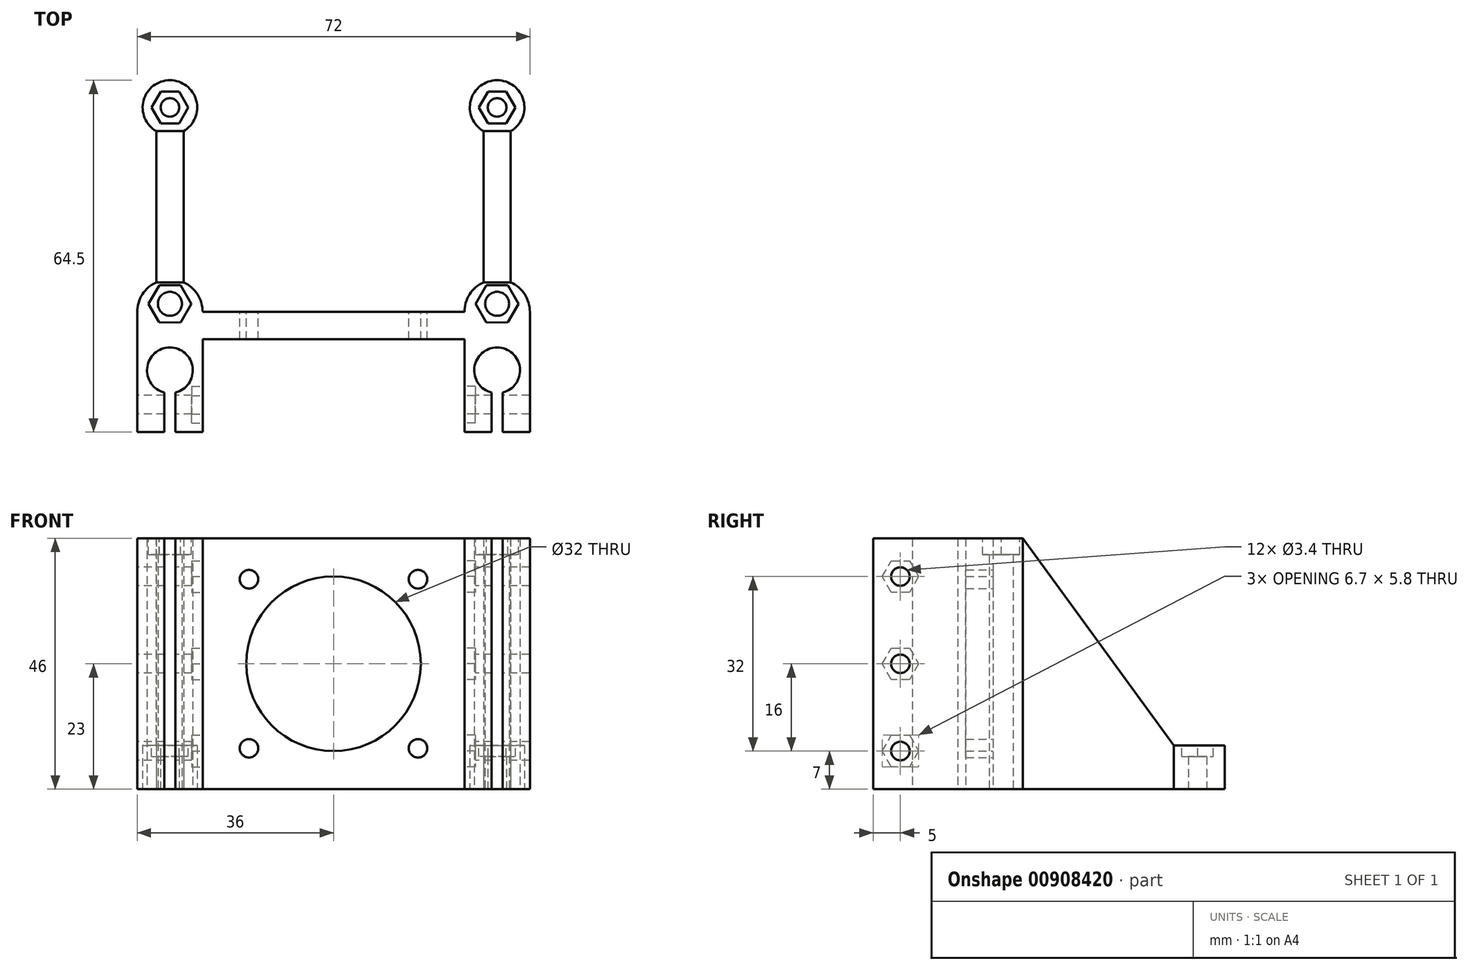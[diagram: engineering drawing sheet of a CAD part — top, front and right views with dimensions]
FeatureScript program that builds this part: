
annotation { "Feature Type Name" : "Feature", "Feature Type Description" : "" }
export const myFeature = defineFeature(function(context is Context, id is Id, definition is map)
    precondition{}
    {
        {
            var Q0;
            Q0=qCreatedBy(makeId("Top.planeOp"),FACE);
            var sketch = newSketch(context, id + "F0", { "sketchPlane" : qUnion([Q0])});
            skArc(sketch, "E0", {"start": v(-29, -14.78) * mm, "mid": v(-30, -6.5) * mm, "end": v(-31, -14.78) * mm});
            skPoint(sketch, "E0.first.point", {"position": v(-31.13, -14.74) * mm});
            skPoint(sketch, "E0.second.point", {"position": v(-34.04, -9.56) * mm});
            skPoint(sketch, "E0.third.point", {"position": v(-26.15, -9.02) * mm});
            skPoint(sketch, "E1.first.point", {"position": v(-36, 0) * mm});
            skLineSegment(sketch, "E2", {"start": v(-36, 0) * mm, "end": v(-36, -22) * mm});
            skLineSegment(sketch, "E3", {"start": v(-36, -22) * mm, "end": v(-31, -22) * mm});
            skLineSegment(sketch, "E4", {"start": v(-31, -22) * mm, "end": v(-31, -14.78) * mm});
            skLineSegment(sketch, "E5", {"start": v(-29, -14.78) * mm, "end": v(-29, -22) * mm});
            skLineSegment(sketch, "E6", {"start": v(-29, -22) * mm, "end": v(-24, -22) * mm});
            skLineSegment(sketch, "E7", {"start": v(0, 0) * mm, "end": v(-24, 0) * mm});
            skLineSegment(sketch, "E8", {"start": v(0, 0) * mm, "end": v(0, -5) * mm});
            skLineSegment(sketch, "E9", {"start": v(0, -5) * mm, "end": v(-24, -5) * mm});
            skLineSegment(sketch, "E10", {"start": v(-24, -5) * mm, "end": v(-24, -22) * mm});
            skLineSegment(sketch, "E11", {"start": v(-30, -10.7) * mm, "end": v(-30, 1.5) * mm, "construction": true});
            skLineSegment(sketch, "E12", {"start": v(-24, 0) * mm, "end": v(-36, 0) * mm, "construction": true});
            skArc(sketch, "E13", {"start": v(-24, 0) * mm, "mid": v(-30, 6) * mm, "end": v(-36, 0) * mm});
            skPoint(sketch, "E14.MirrorP", {"position": v(34.04, -9.56) * mm});
            skLineSegment(sketch, "E15.MirrorCS", {"start": v(0, -5) * mm, "end": v(24, -5) * mm});
            skLineSegment(sketch, "E16.MirrorCS", {"start": v(24, 0) * mm, "end": v(36, 0) * mm, "construction": true});
            skLineSegment(sketch, "E17.MirrorCS", {"start": v(29, -22) * mm, "end": v(24, -22) * mm});
            skPoint(sketch, "E18.MirrorP", {"position": v(26.15, -9.02) * mm});
            skLineSegment(sketch, "E19.MirrorCS", {"start": v(31, -22) * mm, "end": v(31, -14.78) * mm});
            skLineSegment(sketch, "E20.MirrorCS", {"start": v(29, -14.78) * mm, "end": v(29, -22) * mm});
            skPoint(sketch, "E21.MirrorP", {"position": v(31.13, -14.74) * mm});
            skPoint(sketch, "E22.MirrorP", {"position": v(36, 0) * mm});
            skArc(sketch, "E23.MirrorCS", {"start": v(24, 0) * mm, "mid": v(30, 6) * mm, "end": v(36, 0) * mm});
            skArc(sketch, "E24.MirrorC", {"start": v(29, -14.78) * mm, "mid": v(30, -6.5) * mm, "end": v(31, -14.78) * mm});
            skLineSegment(sketch, "E25.MirrorCS", {"start": v(0, 0) * mm, "end": v(24, 0) * mm});
            skLineSegment(sketch, "E26.MirrorCS", {"start": v(24, -5) * mm, "end": v(24, -22) * mm});
            skLineSegment(sketch, "E27.MirrorCS", {"start": v(30, -10.7) * mm, "end": v(30, 1.5) * mm, "construction": true});
            skLineSegment(sketch, "E28.MirrorCS", {"start": v(36, -22) * mm, "end": v(31, -22) * mm});
            skLineSegment(sketch, "E29.MirrorCS", {"start": v(36, 0) * mm, "end": v(36, -22) * mm});
            skCircle(sketch, "E30", {"center": v(-30, 1.5) * mm, "radius": 2.2 * mm});
            skCircle(sketch, "E31.MirrorC", {"center": v(30, 1.5) * mm, "radius": 2.2 * mm});
            skLineSegment(sketch, "E32", {"start": v(-30, 1.5) * mm, "end": v(-30, 46.69) * mm, "construction": true});
            skLineSegment(sketch, "E33", {"start": v(-32.5, 5.45) * mm, "end": v(-32.5, 33.17) * mm});
            skLineSegment(sketch, "E34", {"start": v(-32.5, 33.17) * mm, "end": v(-27.5, 33.17) * mm});
            skLineSegment(sketch, "E35", {"start": v(-27.5, 33.17) * mm, "end": v(-27.5, 5.45) * mm});
            skLineSegment(sketch, "E36", {"start": v(-27.5, 5.45) * mm, "end": v(-32.5, 5.45) * mm, "construction": true});
            skCircle(sketch, "E37", {"center": v(-30, 37.5) * mm, "radius": 1.7 * mm});
            skCircle(sketch, "E38", {"center": v(-30, 37.5) * mm, "radius": 5 * mm});
            skLineSegment(sketch, "E39.MirrorCS", {"start": v(27.5, 33.17) * mm, "end": v(27.5, 5.45) * mm});
            skLineSegment(sketch, "E40.MirrorCS", {"start": v(32.5, 5.45) * mm, "end": v(32.5, 33.17) * mm});
            skCircle(sketch, "E41.MirrorC", {"center": v(30, 37.5) * mm, "radius": 5 * mm});
            skCircle(sketch, "E42.MirrorC", {"center": v(30, 37.5) * mm, "radius": 1.7 * mm});
            skSolve(sketch);
        }
        {
            var Q0;
            Q0=qSketchRegion(id+"F0",true);
            extrude(context, id + "F1", {"entities" : qUnion([Q0]), "depth" : 46 * mm, "offsetDistance" : 25 * mm});
        }
        {
            var Q0;
            Q0=makeQuery(id+"F1.opExtrude","CAP_FACE",FACE,{"disambiguationData":[OSD([sQuery(id+"F0.wireOp",EDGE,"E0"),sQuery(id+"F0.wireOp",EDGE,"E2"),sQuery(id+"F0.wireOp",EDGE,"E3"),sQuery(id+"F0.wireOp",EDGE,"E4"),sQuery(id+"F0.wireOp",EDGE,"E5"),sQuery(id+"F0.wireOp",EDGE,"E6"),sQuery(id+"F0.wireOp",EDGE,"E7"),sQuery(id+"F0.wireOp",EDGE,"E9"),sQuery(id+"F0.wireOp",EDGE,"E10"),sQuery(id+"F0.wireOp",EDGE,"E13"),sQuery(id+"F0.wireOp",EDGE,"E15.MirrorCS"),sQuery(id+"F0.wireOp",EDGE,"E17.MirrorCS"),sQuery(id+"F0.wireOp",EDGE,"E19.MirrorCS"),sQuery(id+"F0.wireOp",EDGE,"E20.MirrorCS"),sQuery(id+"F0.wireOp",EDGE,"E23.MirrorCS"),sQuery(id+"F0.wireOp",EDGE,"E24.MirrorC"),sQuery(id+"F0.wireOp",EDGE,"E25.MirrorCS"),sQuery(id+"F0.wireOp",EDGE,"E26.MirrorCS"),sQuery(id+"F0.wireOp",EDGE,"E28.MirrorCS"),sQuery(id+"F0.wireOp",EDGE,"E29.MirrorCS"),sQuery(id+"F0.wireOp",EDGE,"E30"),sQuery(id+"F0.wireOp",EDGE,"E31.MirrorC")])],"isStart":false});
            var sketch = newSketch(context, id + "F2", { "sketchPlane" : qUnion([Q0])});
            skCircle(sketch, "E43.cCircle", {"center": v(-30, 1.5) * mm, "radius": 3.4 * mm, "construction": true});
            skLineSegment(sketch, "E43.0", {"start": v(-26.07, 1.48) * mm, "end": v(-28.05, -1.9) * mm});
            skLineSegment(sketch, "E43.1", {"start": v(-28.05, -1.9) * mm, "end": v(-31.98, -1.9) * mm});
            skLineSegment(sketch, "E43.2", {"start": v(-31.98, -1.9) * mm, "end": v(-33.93, 1.52) * mm});
            skLineSegment(sketch, "E43.3", {"start": v(-33.93, 1.52) * mm, "end": v(-31.95, 4.9) * mm});
            skLineSegment(sketch, "E43.4", {"start": v(-31.95, 4.9) * mm, "end": v(-28.02, 4.9) * mm});
            skLineSegment(sketch, "E43.5", {"start": v(-28.02, 4.9) * mm, "end": v(-26.07, 1.48) * mm});
            skPoint(sketch, "E43.0.midPoint", {"position": v(-27.06, -0.21) * mm});
            skPoint(sketch, "E44.MirrorP", {"position": v(27.06, -0.21) * mm});
            skLineSegment(sketch, "E45.MirrorCS", {"start": v(31.95, 4.9) * mm, "end": v(28.02, 4.9) * mm});
            skLineSegment(sketch, "E46.MirrorCS", {"start": v(28.05, -1.9) * mm, "end": v(31.98, -1.9) * mm});
            skLineSegment(sketch, "E47.MirrorCS", {"start": v(31.98, -1.9) * mm, "end": v(33.93, 1.52) * mm});
            skCircle(sketch, "E48.MirrorC", {"center": v(30, 1.5) * mm, "radius": 3.4 * mm, "construction": true});
            skLineSegment(sketch, "E49.MirrorCS", {"start": v(26.07, 1.48) * mm, "end": v(28.05, -1.9) * mm});
            skLineSegment(sketch, "E50.MirrorCS", {"start": v(33.93, 1.52) * mm, "end": v(31.95, 4.9) * mm});
            skLineSegment(sketch, "E51.MirrorCS", {"start": v(28.02, 4.9) * mm, "end": v(26.07, 1.48) * mm});
            skSolve(sketch);
        }
        {
            var Q0;
            Q0=qSketchRegion(id+"F2",true);
            extrude(context, id + "F3", {"entities" : qUnion([Q0]), "operationType" : NewBodyOperationType.REMOVE, "oppositeDirection" : true, "depth" : 3 * mm, "offsetDistance" : 25 * mm});
        }
        {
            var Q0;
            Q0=makeQuery(id+"F1.opExtrude","SWEPT_FACE",FACE,{"disambiguationData":[OSD([sQuery(id+"F0.wireOp",EDGE,"E33")])]});
            cPlane(context, id + "F4", {"entities" : qUnion([Q0]), "cplaneType" : CPlaneType.OFFSET, "offset" : 10 * mm, "width" : 150 * mm, "height" : 150 * mm});
        }
        {
            var Q0;
            Q0=qCreatedBy(id+"F4.planeOp",FACE);
            var sketch = newSketch(context, id + "F5", { "sketchPlane" : qUnion([Q0])});
            skLineSegment(sketch, "E52", {"start": v(-43.17, 8) * mm, "end": v(-33.17, 8) * mm});
            skLineSegment(sketch, "E53", {"start": v(-33.17, 8) * mm, "end": v(-5.45, 46) * mm});
            skLineSegment(sketch, "E54", {"start": v(-5.45, 46) * mm, "end": v(-5.45, 46) * mm});
            skLineSegment(sketch, "E55", {"start": v(-5.45, 46) * mm, "end": v(-43.17, 46) * mm});
            skLineSegment(sketch, "E56", {"start": v(-43.17, 46) * mm, "end": v(-43.17, 8) * mm});
            skCircle(sketch, "E57", {"center": v(17, 39) * mm, "radius": 1.7 * mm});
            skCircle(sketch, "E58", {"center": v(17, 23) * mm, "radius": 1.7 * mm});
            skCircle(sketch, "E59", {"center": v(17, 7) * mm, "radius": 1.7 * mm});
            skSolve(sketch);
        }
        {
            var Q0;
            Q0=qSketchRegion(id+"F5",true);
            extrude(context, id + "F6", {"entities" : qUnion([Q0]), "operationType" : NewBodyOperationType.REMOVE, "endBound" : BoundingType.THROUGH_ALL, "oppositeDirection" : true, "depth" : 25 * mm, "offsetDistance" : 25 * mm});
        }
        {
            var Q0;
            Q0=makeQuery(id+"F6.boolean.opBoolean","COPY",FACE,{"disambiguationData":[TD([makeQuery(id+"F1.opExtrude","SWEPT_FACE",FACE,{"disambiguationData":[OSD([sQuery(id+"F0.wireOp",EDGE,"E33")])]})])],"derivedFrom":makeQuery(id+"F6.opExtrude","SWEPT_FACE",FACE,{"disambiguationData":[OSD([sQuery(id+"F5.wireOp",EDGE,"E52")])]})});
            var sketch = newSketch(context, id + "F7", { "sketchPlane" : qUnion([Q0])});
            skCircle(sketch, "E60.cCircle", {"center": v(-30, 37.5) * mm, "radius": 2.9 * mm, "construction": true});
            skLineSegment(sketch, "E60.0", {"start": v(-26.65, 37.5) * mm, "end": v(-28.33, 34.6) * mm});
            skLineSegment(sketch, "E60.1", {"start": v(-28.33, 34.6) * mm, "end": v(-31.67, 34.6) * mm});
            skLineSegment(sketch, "E60.2", {"start": v(-31.67, 34.6) * mm, "end": v(-33.35, 37.5) * mm});
            skLineSegment(sketch, "E60.3", {"start": v(-33.35, 37.5) * mm, "end": v(-31.67, 40.4) * mm});
            skLineSegment(sketch, "E60.4", {"start": v(-31.67, 40.4) * mm, "end": v(-28.33, 40.4) * mm});
            skLineSegment(sketch, "E60.5", {"start": v(-28.33, 40.4) * mm, "end": v(-26.65, 37.5) * mm});
            skPoint(sketch, "E60.0.midPoint", {"position": v(-27.49, 36.05) * mm});
            skLineSegment(sketch, "E61.MirrorCS", {"start": v(26.65, 37.5) * mm, "end": v(28.33, 34.6) * mm});
            skLineSegment(sketch, "E62.MirrorCS", {"start": v(33.35, 37.5) * mm, "end": v(31.67, 40.4) * mm});
            skLineSegment(sketch, "E63.MirrorCS", {"start": v(31.67, 34.6) * mm, "end": v(33.35, 37.5) * mm});
            skLineSegment(sketch, "E64.MirrorCS", {"start": v(31.67, 40.4) * mm, "end": v(28.33, 40.4) * mm});
            skLineSegment(sketch, "E65.MirrorCS", {"start": v(28.33, 34.6) * mm, "end": v(31.67, 34.6) * mm});
            skPoint(sketch, "E66.MirrorP", {"position": v(27.49, 36.05) * mm});
            skCircle(sketch, "E67.MirrorC", {"center": v(30, 37.5) * mm, "radius": 2.9 * mm, "construction": true});
            skLineSegment(sketch, "E68.MirrorCS", {"start": v(28.33, 40.4) * mm, "end": v(26.65, 37.5) * mm});
            skSolve(sketch);
        }
        {
            var Q0;
            Q0=qSketchRegion(id+"F7",true);
            extrude(context, id + "F8", {"entities" : qUnion([Q0]), "operationType" : NewBodyOperationType.REMOVE, "oppositeDirection" : true, "depth" : 2 * mm, "offsetDistance" : 25 * mm});
        }
        {
            var Q0;
            Q0=makeQuery(id+"F1.opExtrude","SWEPT_FACE",FACE,{"disambiguationData":[OSD([sQuery(id+"F0.wireOp",EDGE,"E26.MirrorCS")])]});
            var sketch = newSketch(context, id + "F9", { "sketchPlane" : qUnion([Q0])});
            skCircle(sketch, "E69.cCircle", {"center": v(17, 39) * mm, "radius": 2.9 * mm, "construction": true});
            skLineSegment(sketch, "E69.0", {"start": v(18.67, 36.1) * mm, "end": v(15.33, 36.1) * mm});
            skLineSegment(sketch, "E69.1", {"start": v(15.33, 36.1) * mm, "end": v(13.65, 39) * mm});
            skLineSegment(sketch, "E69.2", {"start": v(13.65, 39) * mm, "end": v(15.33, 41.9) * mm});
            skLineSegment(sketch, "E69.3", {"start": v(15.33, 41.9) * mm, "end": v(18.67, 41.9) * mm});
            skLineSegment(sketch, "E69.4", {"start": v(18.67, 41.9) * mm, "end": v(20.35, 39) * mm});
            skLineSegment(sketch, "E69.5", {"start": v(20.35, 39) * mm, "end": v(18.67, 36.1) * mm});
            skPoint(sketch, "E69.0.midPoint", {"position": v(17, 36.1) * mm});
            skCircle(sketch, "E70.cCircle", {"center": v(17, 23) * mm, "radius": 2.9 * mm, "construction": true});
            skLineSegment(sketch, "E70.0", {"start": v(18.67, 20.1) * mm, "end": v(15.33, 20.1) * mm});
            skLineSegment(sketch, "E70.1", {"start": v(15.33, 20.1) * mm, "end": v(13.65, 23) * mm});
            skLineSegment(sketch, "E70.2", {"start": v(13.65, 23) * mm, "end": v(15.33, 25.9) * mm});
            skLineSegment(sketch, "E70.3", {"start": v(15.33, 25.9) * mm, "end": v(18.67, 25.9) * mm});
            skLineSegment(sketch, "E70.4", {"start": v(18.67, 25.9) * mm, "end": v(20.35, 23) * mm});
            skLineSegment(sketch, "E70.5", {"start": v(20.35, 23) * mm, "end": v(18.67, 20.1) * mm});
            skPoint(sketch, "E70.0.midPoint", {"position": v(17, 20.1) * mm});
            skCircle(sketch, "E71.cCircle", {"center": v(17, 7) * mm, "radius": 2.9 * mm, "construction": true});
            skLineSegment(sketch, "E71.0", {"start": v(18.67, 4.1) * mm, "end": v(15.33, 4.1) * mm});
            skLineSegment(sketch, "E71.1", {"start": v(15.33, 4.1) * mm, "end": v(13.65, 7) * mm});
            skLineSegment(sketch, "E71.2", {"start": v(13.65, 7) * mm, "end": v(15.33, 9.9) * mm});
            skLineSegment(sketch, "E71.3", {"start": v(15.33, 9.9) * mm, "end": v(18.67, 9.9) * mm});
            skLineSegment(sketch, "E71.4", {"start": v(18.67, 9.9) * mm, "end": v(20.35, 7) * mm});
            skLineSegment(sketch, "E71.5", {"start": v(20.35, 7) * mm, "end": v(18.67, 4.1) * mm});
            skPoint(sketch, "E71.0.midPoint", {"position": v(17, 4.1) * mm});
            skSolve(sketch);
        }
        {
            var Q0;
            Q0=qSketchRegion(id+"F9",true);
            extrude(context, id + "F10", {"entities" : qUnion([Q0]), "operationType" : NewBodyOperationType.REMOVE, "oppositeDirection" : true, "depth" : 2 * mm, "offsetDistance" : 25 * mm});
        }
        {
            var Q0;
            Q0=makeQuery(id+"F1.opExtrude","SWEPT_FACE",FACE,{"disambiguationData":[OSD([sQuery(id+"F0.wireOp",EDGE,"E10")])]});
            var sketch = newSketch(context, id + "F11", { "sketchPlane" : qUnion([Q0])});
            skCircle(sketch, "E72.cCircle", {"center": v(-17, 39) * mm, "radius": 2.9 * mm, "construction": true});
            skLineSegment(sketch, "E72.0", {"start": v(-15.33, 36.1) * mm, "end": v(-18.67, 36.1) * mm});
            skLineSegment(sketch, "E72.1", {"start": v(-18.67, 36.1) * mm, "end": v(-20.35, 39) * mm});
            skLineSegment(sketch, "E72.2", {"start": v(-20.35, 39) * mm, "end": v(-18.67, 41.9) * mm});
            skLineSegment(sketch, "E72.3", {"start": v(-18.67, 41.9) * mm, "end": v(-15.33, 41.9) * mm});
            skLineSegment(sketch, "E72.4", {"start": v(-15.33, 41.9) * mm, "end": v(-13.65, 39) * mm});
            skLineSegment(sketch, "E72.5", {"start": v(-13.65, 39) * mm, "end": v(-15.33, 36.1) * mm});
            skPoint(sketch, "E72.0.midPoint", {"position": v(-17, 36.1) * mm});
            skCircle(sketch, "E73.cCircle", {"center": v(-17, 23) * mm, "radius": 2.9 * mm, "construction": true});
            skLineSegment(sketch, "E73.0", {"start": v(-15.33, 20.1) * mm, "end": v(-18.67, 20.1) * mm});
            skLineSegment(sketch, "E73.1", {"start": v(-18.67, 20.1) * mm, "end": v(-20.35, 23) * mm});
            skLineSegment(sketch, "E73.2", {"start": v(-20.35, 23) * mm, "end": v(-18.67, 25.9) * mm});
            skLineSegment(sketch, "E73.3", {"start": v(-18.67, 25.9) * mm, "end": v(-15.33, 25.9) * mm});
            skLineSegment(sketch, "E73.4", {"start": v(-15.33, 25.9) * mm, "end": v(-13.65, 23) * mm});
            skLineSegment(sketch, "E73.5", {"start": v(-13.65, 23) * mm, "end": v(-15.33, 20.1) * mm});
            skPoint(sketch, "E73.0.midPoint", {"position": v(-17, 20.1) * mm});
            skCircle(sketch, "E74.cCircle", {"center": v(-17, 7) * mm, "radius": 2.9 * mm, "construction": true});
            skLineSegment(sketch, "E74.0", {"start": v(-15.33, 4.1) * mm, "end": v(-18.67, 4.1) * mm});
            skLineSegment(sketch, "E74.1", {"start": v(-18.67, 4.1) * mm, "end": v(-20.35, 7) * mm});
            skLineSegment(sketch, "E74.2", {"start": v(-20.35, 7) * mm, "end": v(-18.67, 9.9) * mm});
            skLineSegment(sketch, "E74.3", {"start": v(-18.67, 9.9) * mm, "end": v(-15.33, 9.9) * mm});
            skLineSegment(sketch, "E74.4", {"start": v(-15.33, 9.9) * mm, "end": v(-13.65, 7) * mm});
            skLineSegment(sketch, "E74.5", {"start": v(-13.65, 7) * mm, "end": v(-15.33, 4.1) * mm});
            skPoint(sketch, "E74.0.midPoint", {"position": v(-17, 4.1) * mm});
            skSolve(sketch);
        }
        {
            var Q0;
            Q0=qSketchRegion(id+"F11",true);
            extrude(context, id + "F12", {"entities" : qUnion([Q0]), "operationType" : NewBodyOperationType.REMOVE, "oppositeDirection" : true, "depth" : 2 * mm, "offsetDistance" : 25 * mm});
        }
        {
            var Q0;
            Q0=makeQuery(id+"F1.opExtrude","SWEPT_FACE",FACE,{"disambiguationData":[OSD([sQuery(id+"F0.wireOp",EDGE,"E7"),sQuery(id+"F0.wireOp",EDGE,"E25.MirrorCS")])]});
            var sketch = newSketch(context, id + "F13", { "sketchPlane" : qUnion([Q0])});
            skCircle(sketch, "E75", {"center": v(0, 23) * mm, "radius": 16 * mm});
            skPoint(sketch, "E75.centerSnap0", {"position": v(24, 23) * mm});
            skPoint(sketch, "E76", {"position": v(-15.5, 38.5) * mm});
            skPoint(sketch, "E77", {"position": v(15.5, 38.5) * mm});
            skPoint(sketch, "E78", {"position": v(15.5, 7.5) * mm});
            skPoint(sketch, "E79", {"position": v(-15.5, 7.5) * mm});
            skSolve(sketch);
        }
        {
            var Q0;
            Q0=makeQuery(id+"F13.imprint","IMPRINT",FACE,{"disambiguationData":[TD([[makeQuery(id+"F13.imprint","IMPRINT",EDGE,{"derivedFrom":sQuery(id+"F13.wireOp",EDGE,"E75")}),1.0]])]});
            var Q1;
            Q1=makeQuery(id+"F1.opExtrude","SWEPT_FACE",FACE,{"disambiguationData":[OSD([sQuery(id+"F0.wireOp",EDGE,"E9"),sQuery(id+"F0.wireOp",EDGE,"E15.MirrorCS")])]});
            extrude(context, id + "F14", {"entities" : qUnion([Q0]), "operationType" : NewBodyOperationType.REMOVE, "endBound" : BoundingType.UP_TO_SURFACE, "oppositeDirection" : true, "depth" : 25 * mm, "endBoundEntityFace" : qUnion([Q1]), "offsetDistance" : 25 * mm});
        }
        {
            var Q0;
            Q0=sQuery(id+"F13.wireOp",VERTEX,"E76");
            var Q1;
            Q1=sQuery(id+"F13.wireOp",VERTEX,"E77");
            var Q2;
            Q2=sQuery(id+"F13.wireOp",VERTEX,"E78");
            var Q3;
            Q3=sQuery(id+"F13.wireOp",VERTEX,"E79");
            var Q4;
            Q4=makeQuery(id+"F1.opExtrude","SWEPT_BODY",BODY,{"disambiguationData":[OSD([sQuery(id+"F0.wireOp",EDGE,"E0"),sQuery(id+"F0.wireOp",EDGE,"E2"),sQuery(id+"F0.wireOp",EDGE,"E3"),sQuery(id+"F0.wireOp",EDGE,"E4"),sQuery(id+"F0.wireOp",EDGE,"E5"),sQuery(id+"F0.wireOp",EDGE,"E6"),sQuery(id+"F0.wireOp",EDGE,"E7"),sQuery(id+"F0.wireOp",EDGE,"E9"),sQuery(id+"F0.wireOp",EDGE,"E10"),sQuery(id+"F0.wireOp",EDGE,"E13"),sQuery(id+"F0.wireOp",EDGE,"E15.MirrorCS"),sQuery(id+"F0.wireOp",EDGE,"E17.MirrorCS"),sQuery(id+"F0.wireOp",EDGE,"E19.MirrorCS"),sQuery(id+"F0.wireOp",EDGE,"E20.MirrorCS"),sQuery(id+"F0.wireOp",EDGE,"E23.MirrorCS"),sQuery(id+"F0.wireOp",EDGE,"E24.MirrorC"),sQuery(id+"F0.wireOp",EDGE,"E25.MirrorCS"),sQuery(id+"F0.wireOp",EDGE,"E26.MirrorCS"),sQuery(id+"F0.wireOp",EDGE,"E28.MirrorCS"),sQuery(id+"F0.wireOp",EDGE,"E29.MirrorCS"),sQuery(id+"F0.wireOp",EDGE,"E30"),sQuery(id+"F0.wireOp",EDGE,"E31.MirrorC"),sQuery(id+"F0.wireOp",EDGE,"E33"),sQuery(id+"F0.wireOp",EDGE,"E35"),sQuery(id+"F0.wireOp",EDGE,"E37"),sQuery(id+"F0.wireOp",EDGE,"E38"),sQuery(id+"F0.wireOp",EDGE,"E39.MirrorCS"),sQuery(id+"F0.wireOp",EDGE,"E40.MirrorCS"),sQuery(id+"F0.wireOp",EDGE,"E41.MirrorC"),sQuery(id+"F0.wireOp",EDGE,"E42.MirrorC")])]});
            hole(context, id + "F15", {"style" : HoleStyle.SIMPLE, "endStyle" : HoleEndStyle.THROUGH, "standardTappedOrClearance" : lookupTablePath({ "fit" : "Normal", "standard" : "ISO", "size" : "M3", "type" : "Clearance" }), "standardBlindInLast" : lookupTablePath({ "fit" : "Normal", "standard" : "ISO", "size" : "M3", "type" : "Clearance" }), "holeDiameter" : 3.4 * mm, "majorDiameter" : 5 * mm, "isTappedThrough" : true, "tappedDepth" : 12 * mm, "tapClearance" : 3, "locations" : qUnion([Q0, Q1, Q2, Q3]), "scope" : qUnion([Q4])});
        }
    });
